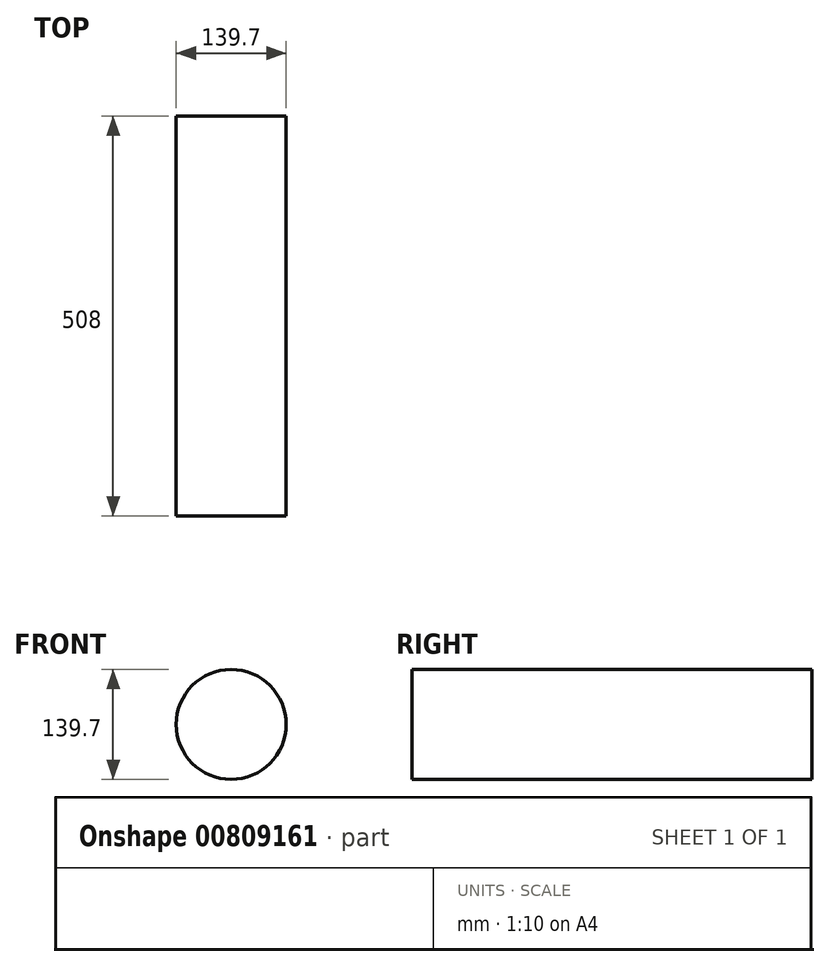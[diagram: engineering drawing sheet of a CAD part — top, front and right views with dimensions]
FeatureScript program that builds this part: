
annotation { "Feature Type Name" : "Feature", "Feature Type Description" : "" }
export const myFeature = defineFeature(function(context is Context, id is Id, definition is map)
    precondition{}
    {
        {
            var Q0;
            Q0=qCreatedBy(makeId("Front.planeOp"),FACE);
            var sketch = newSketch(context, id + "F0", { "sketchPlane" : qUnion([Q0])});
            skCircle(sketch, "E0", {"center": v(0, 2.7) * mm, "radius": 69.85 * mm});
            skSolve(sketch);
        }
        {
            var Q0;
            Q0=makeQuery(id+"F0.imprint","IMPRINT",FACE,{"disambiguationData":[TD([[makeQuery(id+"F0.imprint","IMPRINT",EDGE,{"derivedFrom":sQuery(id+"F0.wireOp",EDGE,"E0")}),1.0]])]});
            extrude(context, id + "F1", {"entities" : qUnion([Q0]), "depth" : 508 * mm, "offsetDistance" : 25.4 * mm});
        }
    });
